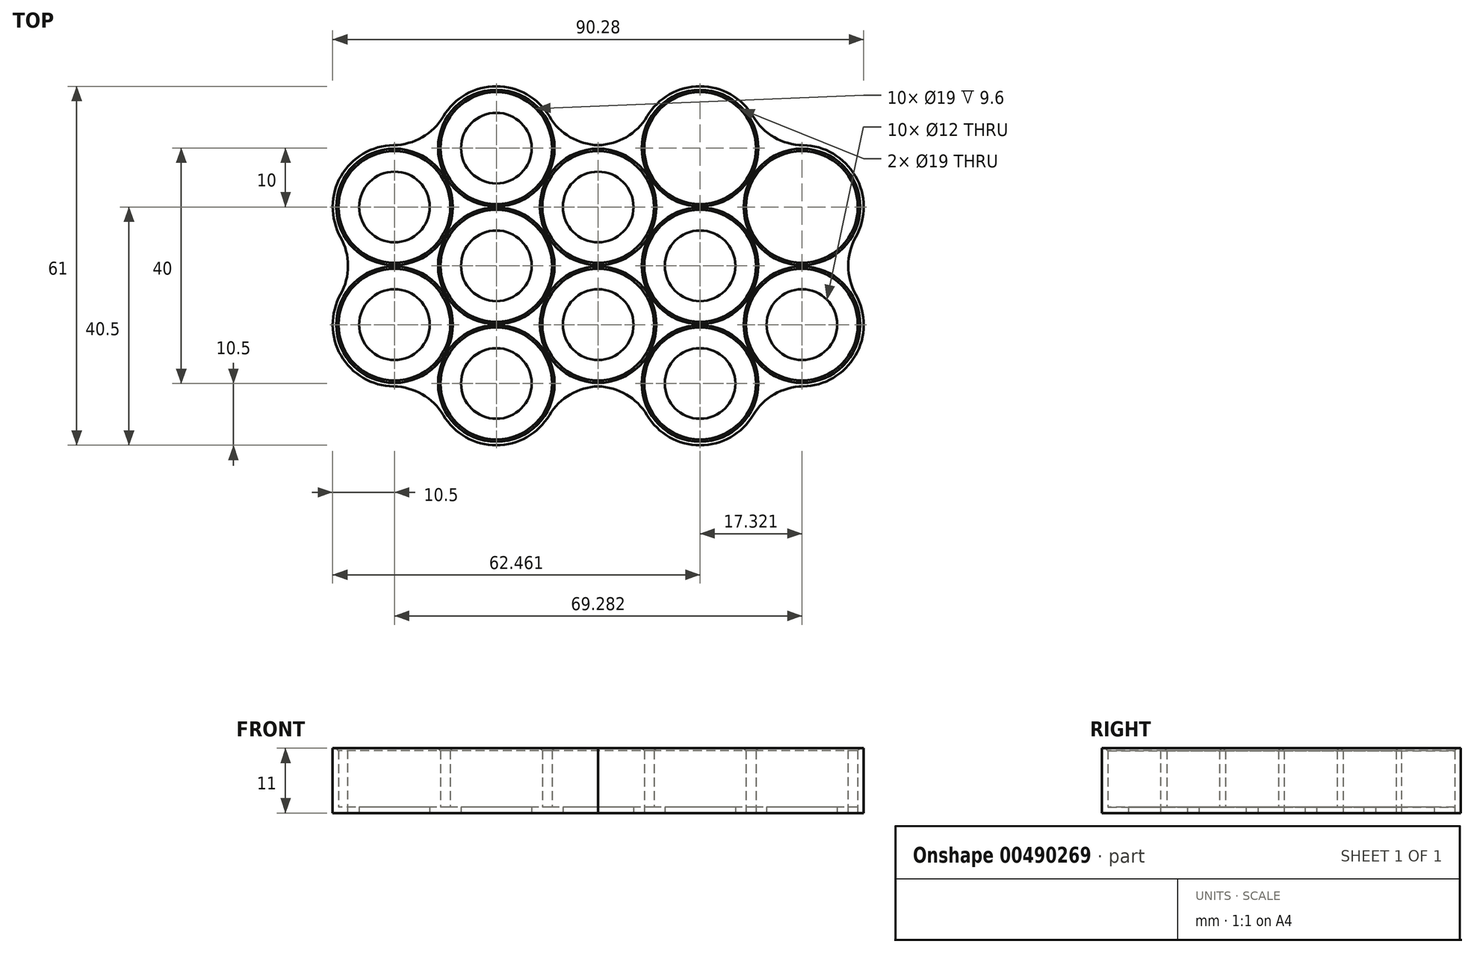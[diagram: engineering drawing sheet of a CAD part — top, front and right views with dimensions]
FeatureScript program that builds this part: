
annotation { "Feature Type Name" : "Feature", "Feature Type Description" : "" }
export const myFeature = defineFeature(function(context is Context, id is Id, definition is map)
    precondition{}
    {
        {
            var Q0;
            Q0=qCreatedBy(makeId("Top.planeOp"),FACE);
            var sketch = newSketch(context, id + "F0", { "sketchPlane" : qUnion([Q0])});
            skCircle(sketch, "E0", {"center": v(0, 0) * mm, "radius": 9.5 * mm});
            skCircle(sketch, "E1", {"center": v(0, 20) * mm, "radius": 9.5 * mm});
            skCircle(sketch, "E2.1.0", {"center": v(-17.32, 10) * mm, "radius": 9.5 * mm});
            skCircle(sketch, "E2.2.0", {"center": v(-17.32, -10) * mm, "radius": 9.5 * mm});
            skCircle(sketch, "E2.3.0", {"center": v(0, -20) * mm, "radius": 9.5 * mm});
            skCircle(sketch, "E2.4.0", {"center": v(17.32, -10) * mm, "radius": 9.5 * mm});
            skCircle(sketch, "E2.5.0", {"center": v(17.32, 10) * mm, "radius": 9.5 * mm});
            skCircle(sketch, "E3", {"center": v(34.64, 0) * mm, "radius": 9.5 * mm});
            skCircle(sketch, "E4", {"center": v(34.64, -20) * mm, "radius": 9.5 * mm});
            skCircle(sketch, "E5", {"center": v(51.96, -10) * mm, "radius": 9.5 * mm});
            skCircle(sketch, "E6.MirrorC", {"center": v(51.96, 10) * mm, "radius": 9.5 * mm});
            skCircle(sketch, "E7.MirrorC", {"center": v(34.64, 20) * mm, "radius": 9.5 * mm});
            skArc(sketch, "E8", {"start": v(-10.26, 17.77) * mm, "mid": v(-26.41, 15.25) * mm, "end": v(-20.52, 0) * mm});
            skArc(sketch, "E9", {"start": v(10.26, 17.77) * mm, "mid": v(0, 30.5) * mm, "end": v(-10.26, 17.77) * mm});
            skArc(sketch, "E10", {"start": v(-20.52, 0) * mm, "mid": v(-26.41, -15.25) * mm, "end": v(-10.26, -17.77) * mm});
            skArc(sketch, "E11", {"start": v(-10.26, -17.77) * mm, "mid": v(0, -30.5) * mm, "end": v(10.26, -17.77) * mm});
            skArc(sketch, "E12", {"start": v(44.9, 17.77) * mm, "mid": v(34.64, 30.5) * mm, "end": v(24.38, 17.77) * mm});
            skArc(sketch, "E13", {"start": v(55.16, 0) * mm, "mid": v(61.05, 15.25) * mm, "end": v(44.9, 17.77) * mm});
            skArc(sketch, "E14", {"start": v(44.9, -17.77) * mm, "mid": v(61.05, -15.25) * mm, "end": v(55.16, 0) * mm});
            skArc(sketch, "E15", {"start": v(24.38, -17.77) * mm, "mid": v(34.64, -30.5) * mm, "end": v(44.9, -17.77) * mm});
            skArc(sketch, "E16", {"start": v(10.26, -17.77) * mm, "mid": v(17.32, -20.5) * mm, "end": v(24.38, -17.77) * mm});
            skArc(sketch, "E17.trimOffspring", {"start": v(24.38, 17.77) * mm, "mid": v(17.32, 20.5) * mm, "end": v(10.26, 17.77) * mm});
            skCircle(sketch, "E18", {"center": v(0, 0) * mm, "radius": 6 * mm});
            skCircle(sketch, "E19", {"center": v(0, 20) * mm, "radius": 6 * mm});
            skCircle(sketch, "E20.1.0", {"center": v(-17.32, 10) * mm, "radius": 6 * mm});
            skCircle(sketch, "E20.2.0", {"center": v(-17.32, -10) * mm, "radius": 6 * mm});
            skCircle(sketch, "E20.3.0", {"center": v(0, -20) * mm, "radius": 6 * mm});
            skCircle(sketch, "E20.4.0", {"center": v(17.32, -10) * mm, "radius": 6 * mm});
            skCircle(sketch, "E20.5.0", {"center": v(17.32, 10) * mm, "radius": 6 * mm});
            skCircle(sketch, "E21", {"center": v(34.64, 0) * mm, "radius": 6 * mm});
            skCircle(sketch, "E22", {"center": v(34.64, 20) * mm, "radius": 6 * mm});
            skCircle(sketch, "E23", {"center": v(51.96, 10) * mm, "radius": 6 * mm});
            skCircle(sketch, "E24", {"center": v(51.96, -10) * mm, "radius": 6 * mm});
            skCircle(sketch, "E25", {"center": v(34.64, -20) * mm, "radius": 6 * mm});
            skSolve(sketch);
        }
        {
            var Q0;
            Q0=makeQuery(id+"F0.imprint","IMPRINT",FACE,{"disambiguationData":[TD([[makeQuery(id+"F0.imprint","IMPRINT",EDGE,{"derivedFrom":sQuery(id+"F0.wireOp",EDGE,"E0")}),-1.0]])]});
            extrude(context, id + "F1", {"entities" : qUnion([Q0]), "depth" : 11 * mm, "offsetDistance" : 25 * mm});
        }
        {
            var Q0;
            Q0=makeQuery(id+"F0.imprint","IMPRINT",FACE,{"disambiguationData":[TD([[makeQuery(id+"F0.imprint","IMPRINT",EDGE,{"derivedFrom":sQuery(id+"F0.wireOp",EDGE,"E1")}),1.0]])]});
            var Q1;
            Q1=makeQuery(id+"F0.imprint","IMPRINT",FACE,{"disambiguationData":[TD([[makeQuery(id+"F0.imprint","IMPRINT",EDGE,{"derivedFrom":sQuery(id+"F0.wireOp",EDGE,"E2.1.0")}),1.0]])]});
            var Q2;
            Q2=makeQuery(id+"F0.imprint","IMPRINT",FACE,{"disambiguationData":[TD([[makeQuery(id+"F0.imprint","IMPRINT",EDGE,{"derivedFrom":sQuery(id+"F0.wireOp",EDGE,"E2.2.0")}),1.0]])]});
            var Q3;
            Q3=makeQuery(id+"F0.imprint","IMPRINT",FACE,{"disambiguationData":[TD([[makeQuery(id+"F0.imprint","IMPRINT",EDGE,{"derivedFrom":sQuery(id+"F0.wireOp",EDGE,"E0")}),1.0]])]});
            var Q4;
            Q4=makeQuery(id+"F0.imprint","IMPRINT",FACE,{"disambiguationData":[TD([[makeQuery(id+"F0.imprint","IMPRINT",EDGE,{"derivedFrom":sQuery(id+"F0.wireOp",EDGE,"E2.3.0")}),1.0]])]});
            var Q5;
            Q5=makeQuery(id+"F0.imprint","IMPRINT",FACE,{"disambiguationData":[TD([[makeQuery(id+"F0.imprint","IMPRINT",EDGE,{"derivedFrom":sQuery(id+"F0.wireOp",EDGE,"E2.4.0")}),1.0]])]});
            var Q6;
            Q6=makeQuery(id+"F0.imprint","IMPRINT",FACE,{"disambiguationData":[TD([[makeQuery(id+"F0.imprint","IMPRINT",EDGE,{"derivedFrom":sQuery(id+"F0.wireOp",EDGE,"E2.5.0")}),1.0]])]});
            var Q7;
            Q7=makeQuery(id+"F0.imprint","IMPRINT",FACE,{"disambiguationData":[TD([[makeQuery(id+"F0.imprint","IMPRINT",EDGE,{"derivedFrom":sQuery(id+"F0.wireOp",EDGE,"E7.MirrorC")}),-1.0]])]});
            var Q8;
            Q8=makeQuery(id+"F0.imprint","IMPRINT",FACE,{"disambiguationData":[TD([[makeQuery(id+"F0.imprint","IMPRINT",EDGE,{"derivedFrom":sQuery(id+"F0.wireOp",EDGE,"E3")}),1.0]])]});
            var Q9;
            Q9=makeQuery(id+"F0.imprint","IMPRINT",FACE,{"disambiguationData":[TD([[makeQuery(id+"F0.imprint","IMPRINT",EDGE,{"derivedFrom":sQuery(id+"F0.wireOp",EDGE,"E4")}),1.0]])]});
            var Q10;
            Q10=makeQuery(id+"F0.imprint","IMPRINT",FACE,{"disambiguationData":[TD([[makeQuery(id+"F0.imprint","IMPRINT",EDGE,{"derivedFrom":sQuery(id+"F0.wireOp",EDGE,"E5")}),1.0]])]});
            var Q11;
            Q11=makeQuery(id+"F0.imprint","IMPRINT",FACE,{"disambiguationData":[TD([[makeQuery(id+"F0.imprint","IMPRINT",EDGE,{"derivedFrom":sQuery(id+"F0.wireOp",EDGE,"E6.MirrorC")}),-1.0]])]});
            extrude(context, id + "F2", {"entities" : qUnion([Q0, Q1, Q2, Q3, Q4, Q5, Q6, Q7, Q8, Q9, Q10, Q11]), "operationType" : NewBodyOperationType.ADD, "depth" : 1 * mm});
        }
        {
            var Q0;
            Q0=makeQuery(id+"F1.opExtrude","SWEPT_EDGE",EDGE,{"disambiguationData":[OSD([sQuery(id+"F0.wireOp",EDGE,"E12"),sQuery(id+"F0.wireOp",EDGE,"E17.trimOffspring")])]});
            var Q1;
            Q1=makeQuery(id+"F1.opExtrude","SWEPT_EDGE",EDGE,{"disambiguationData":[OSD([sQuery(id+"F0.wireOp",EDGE,"E9"),sQuery(id+"F0.wireOp",EDGE,"E17.trimOffspring")])]});
            var Q2;
            Q2=makeQuery(id+"F1.opExtrude","SWEPT_EDGE",EDGE,{"disambiguationData":[OSD([sQuery(id+"F0.wireOp",EDGE,"E8"),sQuery(id+"F0.wireOp",EDGE,"E9")])]});
            var Q3;
            Q3=makeQuery(id+"F1.opExtrude","SWEPT_EDGE",EDGE,{"disambiguationData":[OSD([sQuery(id+"F0.wireOp",EDGE,"E8"),sQuery(id+"F0.wireOp",EDGE,"E10")])]});
            var Q4;
            Q4=makeQuery(id+"F1.opExtrude","SWEPT_EDGE",EDGE,{"disambiguationData":[OSD([sQuery(id+"F0.wireOp",EDGE,"E10"),sQuery(id+"F0.wireOp",EDGE,"E11")])]});
            var Q5;
            Q5=makeQuery(id+"F1.opExtrude","SWEPT_EDGE",EDGE,{"disambiguationData":[OSD([sQuery(id+"F0.wireOp",EDGE,"E11"),sQuery(id+"F0.wireOp",EDGE,"E16")])]});
            var Q6;
            Q6=makeQuery(id+"F1.opExtrude","SWEPT_EDGE",EDGE,{"disambiguationData":[OSD([sQuery(id+"F0.wireOp",EDGE,"E15"),sQuery(id+"F0.wireOp",EDGE,"E16")])]});
            var Q7;
            Q7=makeQuery(id+"F1.opExtrude","SWEPT_EDGE",EDGE,{"disambiguationData":[OSD([sQuery(id+"F0.wireOp",EDGE,"E14"),sQuery(id+"F0.wireOp",EDGE,"E15")])]});
            var Q8;
            Q8=makeQuery(id+"F1.opExtrude","SWEPT_EDGE",EDGE,{"disambiguationData":[OSD([sQuery(id+"F0.wireOp",EDGE,"E13"),sQuery(id+"F0.wireOp",EDGE,"E14")])]});
            var Q9;
            Q9=makeQuery(id+"F1.opExtrude","SWEPT_EDGE",EDGE,{"disambiguationData":[OSD([sQuery(id+"F0.wireOp",EDGE,"E12"),sQuery(id+"F0.wireOp",EDGE,"E13")])]});
            fillet(context, id + "F3", {"entities" : qUnion([Q0, Q1, Q2, Q3, Q4, Q5, Q6, Q7, Q8, Q9]), "radius" : 10 * mm, "tangentPropagation" : true, "allowEdgeOverflow" : false});
        }
        {
            var Q0;
            Q0=makeQuery(id+"F1.opExtrude","CAP_EDGE",EDGE,{"disambiguationData":[OSD([sQuery(id+"F0.wireOp",EDGE,"E2.1.0")])],"isStart":false});
            var Q1;
            Q1=makeQuery(id+"F1.opExtrude","CAP_EDGE",EDGE,{"disambiguationData":[OSD([sQuery(id+"F0.wireOp",EDGE,"E1")])],"isStart":false});
            var Q2;
            Q2=makeQuery(id+"F1.opExtrude","CAP_EDGE",EDGE,{"disambiguationData":[OSD([sQuery(id+"F0.wireOp",EDGE,"E2.2.0")])],"isStart":false});
            var Q3;
            Q3=makeQuery(id+"F1.opExtrude","CAP_EDGE",EDGE,{"disambiguationData":[OSD([sQuery(id+"F0.wireOp",EDGE,"E0")])],"isStart":false});
            var Q4;
            Q4=makeQuery(id+"F1.opExtrude","CAP_EDGE",EDGE,{"disambiguationData":[OSD([sQuery(id+"F0.wireOp",EDGE,"E2.3.0")])],"isStart":false});
            var Q5;
            Q5=makeQuery(id+"F1.opExtrude","CAP_EDGE",EDGE,{"disambiguationData":[OSD([sQuery(id+"F0.wireOp",EDGE,"E2.4.0")])],"isStart":false});
            var Q6;
            Q6=makeQuery(id+"F1.opExtrude","CAP_EDGE",EDGE,{"disambiguationData":[OSD([sQuery(id+"F0.wireOp",EDGE,"E2.5.0")])],"isStart":false});
            var Q7;
            Q7=makeQuery(id+"F1.opExtrude","CAP_EDGE",EDGE,{"disambiguationData":[OSD([sQuery(id+"F0.wireOp",EDGE,"E7.MirrorC")])],"isStart":false});
            var Q8;
            Q8=makeQuery(id+"F1.opExtrude","CAP_EDGE",EDGE,{"disambiguationData":[OSD([sQuery(id+"F0.wireOp",EDGE,"E3")])],"isStart":false});
            var Q9;
            Q9=makeQuery(id+"F1.opExtrude","CAP_EDGE",EDGE,{"disambiguationData":[OSD([sQuery(id+"F0.wireOp",EDGE,"E6.MirrorC")])],"isStart":false});
            var Q10;
            Q10=makeQuery(id+"F1.opExtrude","CAP_EDGE",EDGE,{"disambiguationData":[OSD([sQuery(id+"F0.wireOp",EDGE,"E5")])],"isStart":false});
            var Q11;
            Q11=makeQuery(id+"F1.opExtrude","CAP_EDGE",EDGE,{"disambiguationData":[OSD([sQuery(id+"F0.wireOp",EDGE,"E4")])],"isStart":false});
            chamfer(context, id + "F4", {"entities" : qUnion([Q0, Q1, Q2, Q3, Q4, Q5, Q6, Q7, Q8, Q9, Q10, Q11]), "width" : 0.4 * mm, "tangentPropagation" : true});
        }
    });
